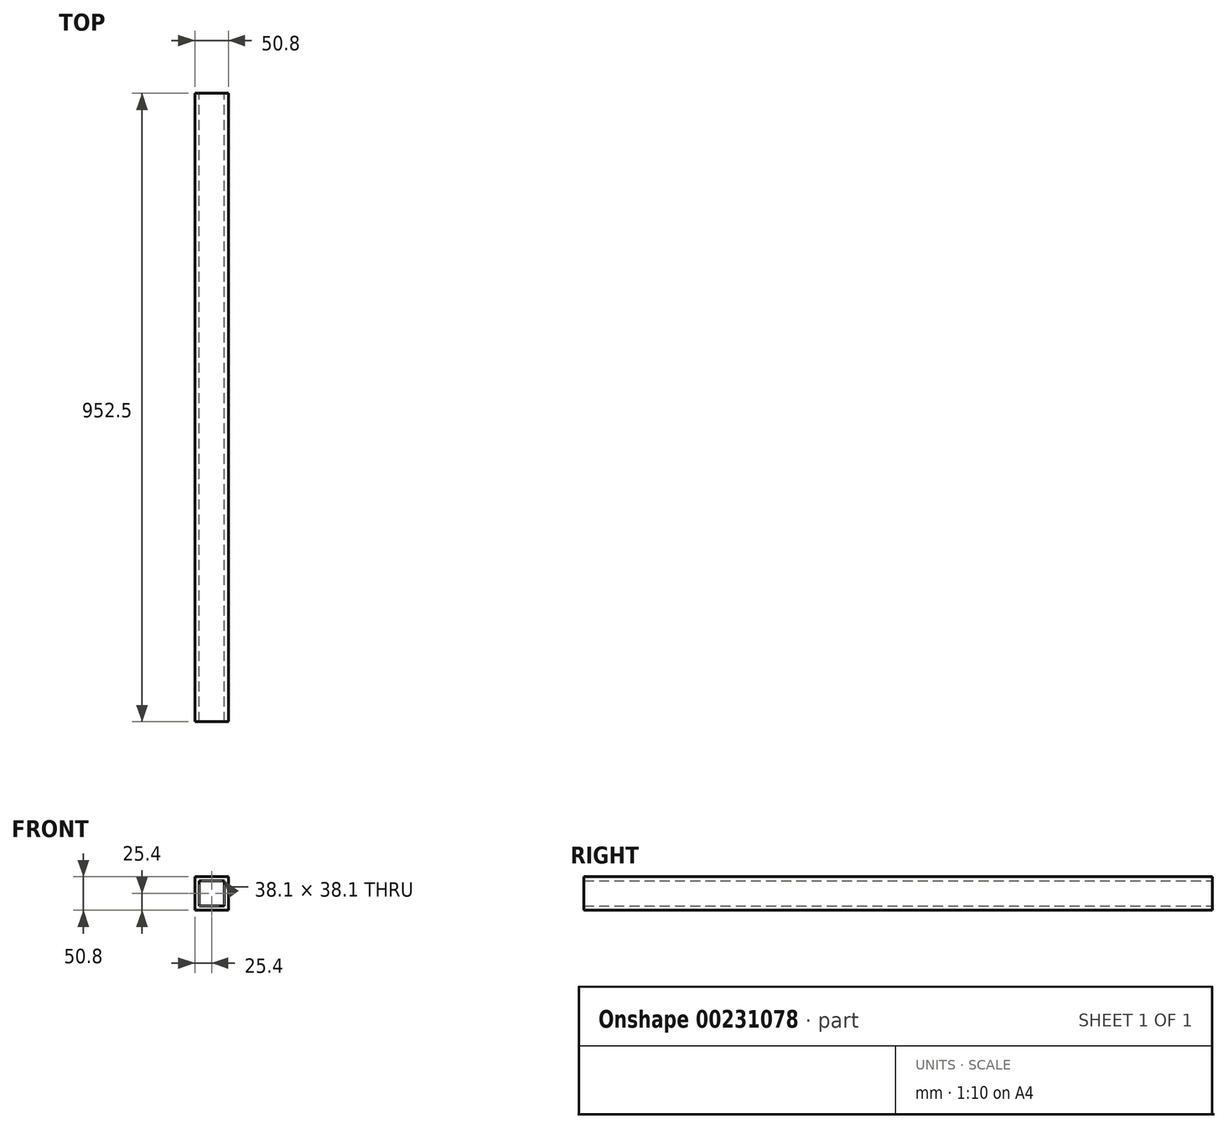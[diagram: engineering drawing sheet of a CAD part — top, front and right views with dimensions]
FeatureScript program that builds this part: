
annotation { "Feature Type Name" : "Feature", "Feature Type Description" : "" }
export const myFeature = defineFeature(function(context is Context, id is Id, definition is map)
    precondition{}
    {
        {
            var Q0;
            Q0=qCreatedBy(makeId("Front.planeOp"),FACE);
            var sketch = newSketch(context, id + "F0", { "sketchPlane" : qUnion([Q0])});
            skLineSegment(sketch, "E0.bottom", {"start": v(0, 0) * mm, "end": v(50.8, 0) * mm});
            skLineSegment(sketch, "E0.top", {"start": v(0, 50.8) * mm, "end": v(50.8, 50.8) * mm});
            skLineSegment(sketch, "E0.left", {"start": v(0, 0) * mm, "end": v(0, 50.8) * mm});
            skLineSegment(sketch, "E0.right", {"start": v(50.8, 0) * mm, "end": v(50.8, 50.8) * mm});
            skLineSegment(sketch, "E1.0", {"start": v(6.35, 44.45) * mm, "end": v(44.45, 44.45) * mm});
            skLineSegment(sketch, "E1.1", {"start": v(6.35, 6.35) * mm, "end": v(6.35, 44.45) * mm});
            skLineSegment(sketch, "E1.2", {"start": v(6.35, 6.35) * mm, "end": v(44.45, 6.35) * mm});
            skLineSegment(sketch, "E1.3", {"start": v(44.45, 6.35) * mm, "end": v(44.45, 44.45) * mm});
            skSolve(sketch);
        }
        {
            var Q0;
            Q0 = qSketchRegion(id + "F0", true);
            extrude(context, id + "F1", {"entities" : qUnion([Q0]), "depth" : 952.5 * mm});
        }
    });
